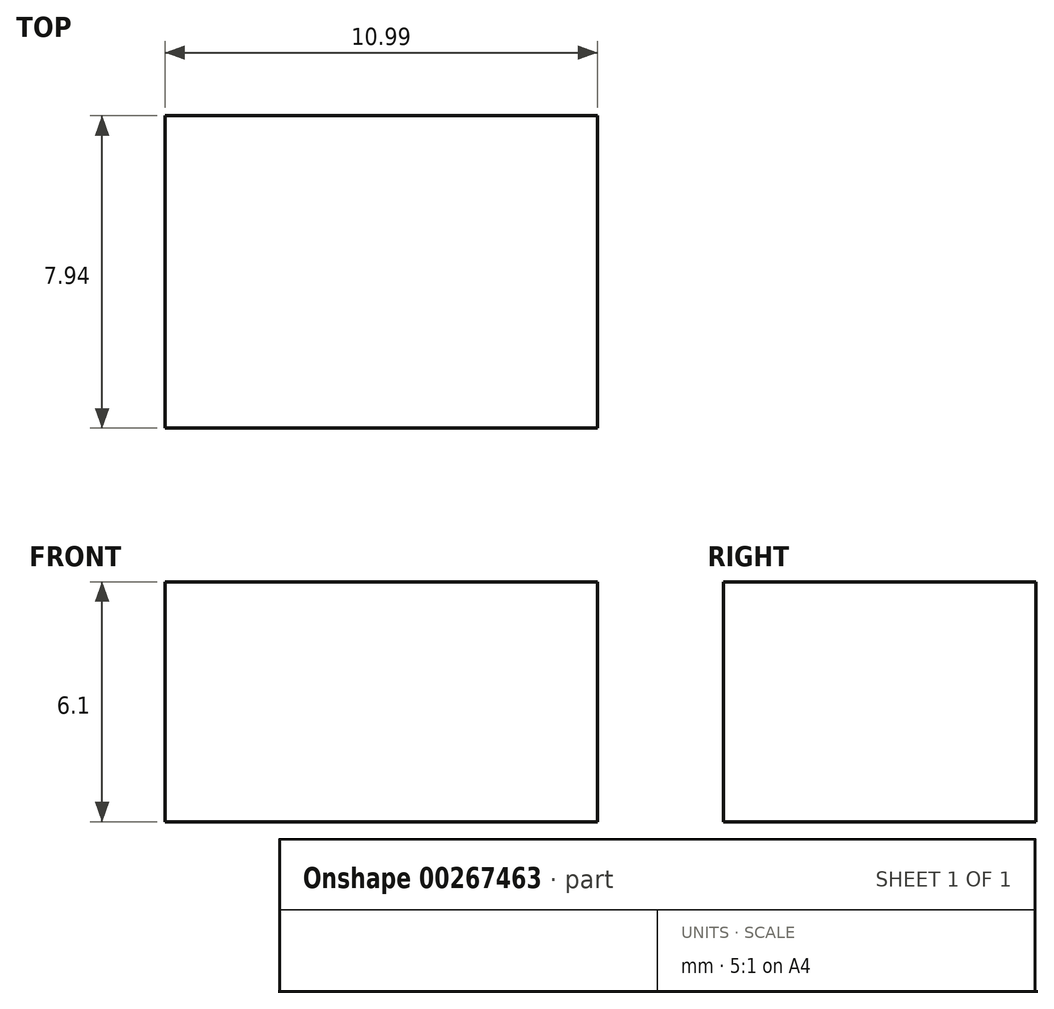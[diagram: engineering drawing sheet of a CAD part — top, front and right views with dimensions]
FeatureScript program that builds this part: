
annotation { "Feature Type Name" : "Feature", "Feature Type Description" : "" }
export const myFeature = defineFeature(function(context is Context, id is Id, definition is map)
    precondition{}
    {
        {
            var Q0;
            Q0=qCreatedBy(makeId("Top.planeOp"),FACE);
            var sketch = newSketch(context, id + "F0", { "sketchPlane" : qUnion([Q0])});
            skLineSegment(sketch, "E0.bottom", {"start": v(-43.65, 37.85) * mm, "end": v(-54.64, 37.85) * mm});
            skLineSegment(sketch, "E0.top", {"start": v(-43.65, 45.8) * mm, "end": v(-54.64, 45.8) * mm});
            skLineSegment(sketch, "E0.left", {"start": v(-43.65, 37.85) * mm, "end": v(-43.65, 45.8) * mm});
            skLineSegment(sketch, "E0.right", {"start": v(-54.64, 37.85) * mm, "end": v(-54.64, 45.8) * mm});
            skPoint(sketch, "E0.middle", {"position": v(-49.15, 41.82) * mm});
            skSolve(sketch);
        }
        {
            var Q0;
            Q0 = qSketchRegion(id + "F0", true);
            extrude(context, id + "F1", {"entities" : qUnion([Q0]), "depth" : 6.1 * mm});
        }
    });
